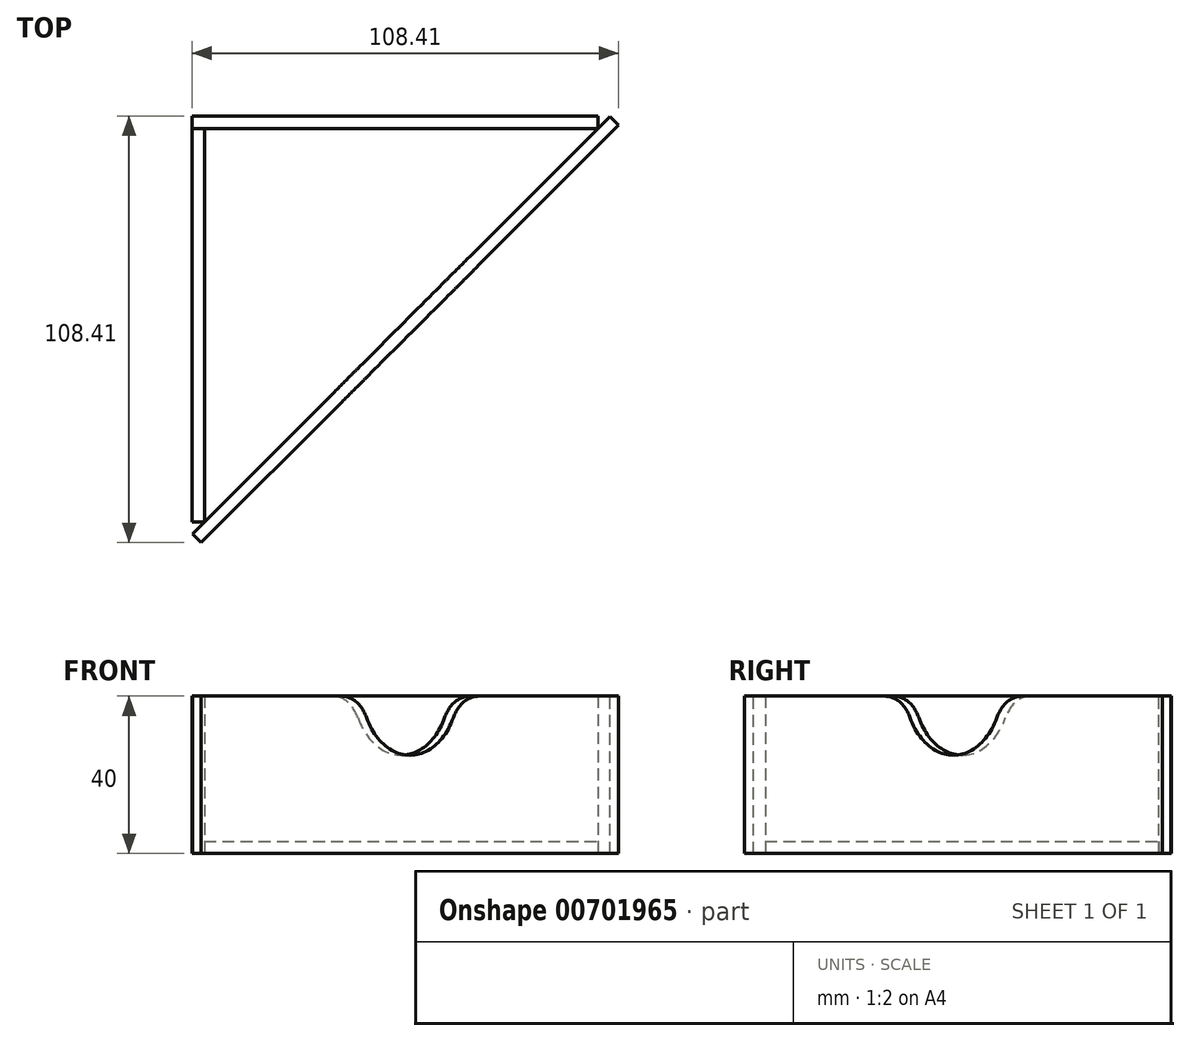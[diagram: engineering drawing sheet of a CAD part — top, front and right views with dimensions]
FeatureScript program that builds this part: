
annotation { "Feature Type Name" : "Feature", "Feature Type Description" : "" }
export const myFeature = defineFeature(function(context is Context, id is Id, definition is map)
    precondition{}
    {
        {
            assignVariable(context, id + "F0", {"name" : "x", "anyValue" : 3.15});
        }
        {
            var Q0;
            Q0=qCreatedBy(makeId("Top.planeOp"),FACE);
            var sketch = newSketch(context, id + "F1", { "sketchPlane" : qUnion([Q0])});
            skLineSegment(sketch, "E0", {"start": v(0, 0) * mm, "end": v(0, 100) * mm});
            skLineSegment(sketch, "E1", {"start": v(0, 100) * mm, "end": v(100, 100) * mm});
            skLineSegment(sketch, "E2", {"start": v(0, 0) * mm, "end": v(100, 100) * mm});
            skLineSegment(sketch, "E3.bottom", {"start": v(-6.3, -13.7) * mm, "end": v(3.7, -13.7) * mm, "construction": true});
            skLineSegment(sketch, "E3.top", {"start": v(-6.3, 106.3) * mm, "end": v(113.7, 106.3) * mm, "construction": true});
            skLineSegment(sketch, "E3.left", {"start": v(-6.3, -13.7) * mm, "end": v(-6.3, 106.3) * mm, "construction": true});
            skLineSegment(sketch, "E3.right", {"start": v(113.7, 96.3) * mm, "end": v(113.7, 106.3) * mm, "construction": true});
            skLineSegment(sketch, "E4", {"start": v(3.7, -13.7) * mm, "end": v(113.7, 96.3) * mm, "construction": true});
            skLineSegment(sketch, "E5", {"start": v(0, 0) * mm, "end": v(-6.3, -6.3) * mm, "construction": true});
            skLineSegment(sketch, "E6", {"start": v(100, 100) * mm, "end": v(106.3, 106.3) * mm, "construction": true});
            skSolve(sketch);
        }
        {
            var Q0;
            Q0 = qSketchRegion(id + "F1", true);
            extrude(context, id + "F2", {"entities" : qUnion([Q0]), "depth" : (getVariable(context, 'x')) * mm, "offsetDistance" : 25 * mm});
        }
        {
            var Q0;
            Q0=makeQuery(id+"F2.opExtrude","SWEPT_FACE",FACE,{"disambiguationData":[OSD([sQuery(id+"F1.wireOp",EDGE,"E0")])]});
            var sketch = newSketch(context, id + "F3", { "sketchPlane" : qUnion([Q0])});
            skLineSegment(sketch, "E7.bottom", {"start": v(-100, 0) * mm, "end": v(0, 0) * mm});
            skLineSegment(sketch, "E7.top", {"start": v(-100, 40) * mm, "end": v(0, 40) * mm});
            skLineSegment(sketch, "E7.left", {"start": v(-100, 0) * mm, "end": v(-100, 40) * mm});
            skLineSegment(sketch, "E7.right", {"start": v(0, 0) * mm, "end": v(0, 40) * mm});
            skSolve(sketch);
        }
        {
            var Q0;
            Q0 = qSketchRegion(id + "F3", true);
            extrude(context, id + "F4", {"entities" : qUnion([Q0]), "depth" : (getVariable(context, 'x')) * mm, "offsetDistance" : 25 * mm});
        }
        {
            var Q0;
            Q0=makeQuery(id+"F2.opExtrude","SWEPT_FACE",FACE,{"disambiguationData":[OSD([sQuery(id+"F1.wireOp",EDGE,"E1")])]});
            var sketch = newSketch(context, id + "F5", { "sketchPlane" : qUnion([Q0])});
            skLineSegment(sketch, "E8.bottom", {"start": v(-100, 0) * mm, "end": v(3.15, 0) * mm});
            skLineSegment(sketch, "E8.top", {"start": v(-100, 40) * mm, "end": v(3.15, 40) * mm});
            skLineSegment(sketch, "E8.left", {"start": v(-100, 0) * mm, "end": v(-100, 40) * mm});
            skLineSegment(sketch, "E8.right", {"start": v(3.15, 0) * mm, "end": v(3.15, 40) * mm});
            skSolve(sketch);
        }
        {
            var Q0;
            Q0 = qSketchRegion(id + "F5", true);
            extrude(context, id + "F6", {"entities" : qUnion([Q0]), "depth" : (getVariable(context, 'x')) * mm, "offsetDistance" : 25 * mm});
        }
        {
            var Q0;
            Q0=makeQuery(id+"F2.opExtrude","SWEPT_FACE",FACE,{"disambiguationData":[OSD([sQuery(id+"F1.wireOp",EDGE,"E2")])]});
            var sketch = newSketch(context, id + "F7", { "sketchPlane" : qUnion([Q0])});
            skLineSegment(sketch, "E9.bottom", {"start": v(-4.29, 0) * mm, "end": v(145.71, 0) * mm});
            skLineSegment(sketch, "E9.top", {"start": v(-4.29, 40) * mm, "end": v(145.71, 40) * mm});
            skLineSegment(sketch, "E9.left", {"start": v(-4.29, 0) * mm, "end": v(-4.29, 40) * mm});
            skLineSegment(sketch, "E9.right", {"start": v(145.71, 0) * mm, "end": v(145.71, 40) * mm});
            skPoint(sketch, "E10", {"position": v(70.71, 0) * mm});
            skSolve(sketch);
        }
        {
            var Q0;
            Q0 = qSketchRegion(id + "F7", true);
            extrude(context, id + "F8", {"entities" : qUnion([Q0]), "depth" : (getVariable(context, 'x')) * mm, "offsetDistance" : 25 * mm});
        }
        {
            var Q0;
            Q0=makeQuery(id+"F8.opExtrude","CAP_FACE",FACE,{"disambiguationData":[OSD([sQuery(id+"F7.wireOp",EDGE,"E9.bottom"),sQuery(id+"F7.wireOp",EDGE,"E9.top"),sQuery(id+"F7.wireOp",EDGE,"E9.left"),sQuery(id+"F7.wireOp",EDGE,"E9.right")])],"isStart":false});
            var sketch = newSketch(context, id + "F9", { "sketchPlane" : qUnion([Q0])});
            skCircle(sketch, "E11", {"center": v(70.71, 42.5) * mm, "radius": 17.5 * mm});
            skPoint(sketch, "E11.centerSnap0", {"position": v(70.71, 40) * mm});
            skSolve(sketch);
        }
        {
            var Q0;
            Q0 = qSketchRegion(id + "F9", true);
            extrude(context, id + "F10", {"entities" : qUnion([Q0]), "operationType" : NewBodyOperationType.REMOVE, "oppositeDirection" : true, "depth" : 25 * mm, "offsetDistance" : 25 * mm});
        }
        {
            var Q0;
            Q0=makeQuery(id+"F10.boolean.opBoolean","INTERSECT",EDGE,{"disambiguationData":[OD(0.0)],"derivedFrom":[makeQuery(id+"F8.opExtrude","SWEPT_FACE",FACE,{"disambiguationData":[OSD([sQuery(id+"F7.wireOp",EDGE,"E9.top")])]}),makeQuery(id+"F10.opExtrude","SWEPT_FACE",FACE,{"disambiguationData":[OSD([sQuery(id+"F9.wireOp",EDGE,"E11")])]})]});
            var Q1;
            Q1=makeQuery(id+"F10.boolean.opBoolean","INTERSECT",EDGE,{"disambiguationData":[OD(1.0)],"derivedFrom":[makeQuery(id+"F8.opExtrude","SWEPT_FACE",FACE,{"disambiguationData":[OSD([sQuery(id+"F7.wireOp",EDGE,"E9.top")])]}),makeQuery(id+"F10.opExtrude","SWEPT_FACE",FACE,{"disambiguationData":[OSD([sQuery(id+"F9.wireOp",EDGE,"E11")])]})]});
            fillet(context, id + "F11", {"entities" : qUnion([Q0, Q1]), "radius" : 10 * mm, "tangentPropagation" : true, "allowEdgeOverflow" : false});
        }
    });
